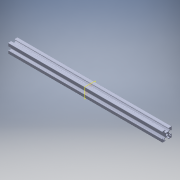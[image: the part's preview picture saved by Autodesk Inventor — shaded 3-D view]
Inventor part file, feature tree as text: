
AUTODESK INVENTOR PART (.ipt)
format: ipt  version: 2018 (Build 220112000, 112)  size: 375,808 bytes
history: native  units: in
note: dims shown in document units (in); Inventor stores cm internally (conversion verified against a paired STEP export)
features: extrude x1, plane x1, sketch x1, projected_geometry x1, fillet x1
ambient origin geometry x8: Origin, YZ Plane, XZ Plane, XY Plane, X Axis, Y Axis, Z Axis, Center Point
bodies: Solid1 (feature_tree)
feature tree (5):
  extrude  "Extrusion2"  [1 undecoded]
  plane  "Work Plane1"
  sketch  "Sketch3"  dims[d2=8.6614in d3=0.0in]
  projected_geometry  "Projected Loop2"
  fillet  "Fillet5"  [1 undecoded]
note: 2 required parameter values undecoded (feature->parameter linkage not recoverable at this tier; creation-order binding heuristic only, values carry confidence <= 0.55)
